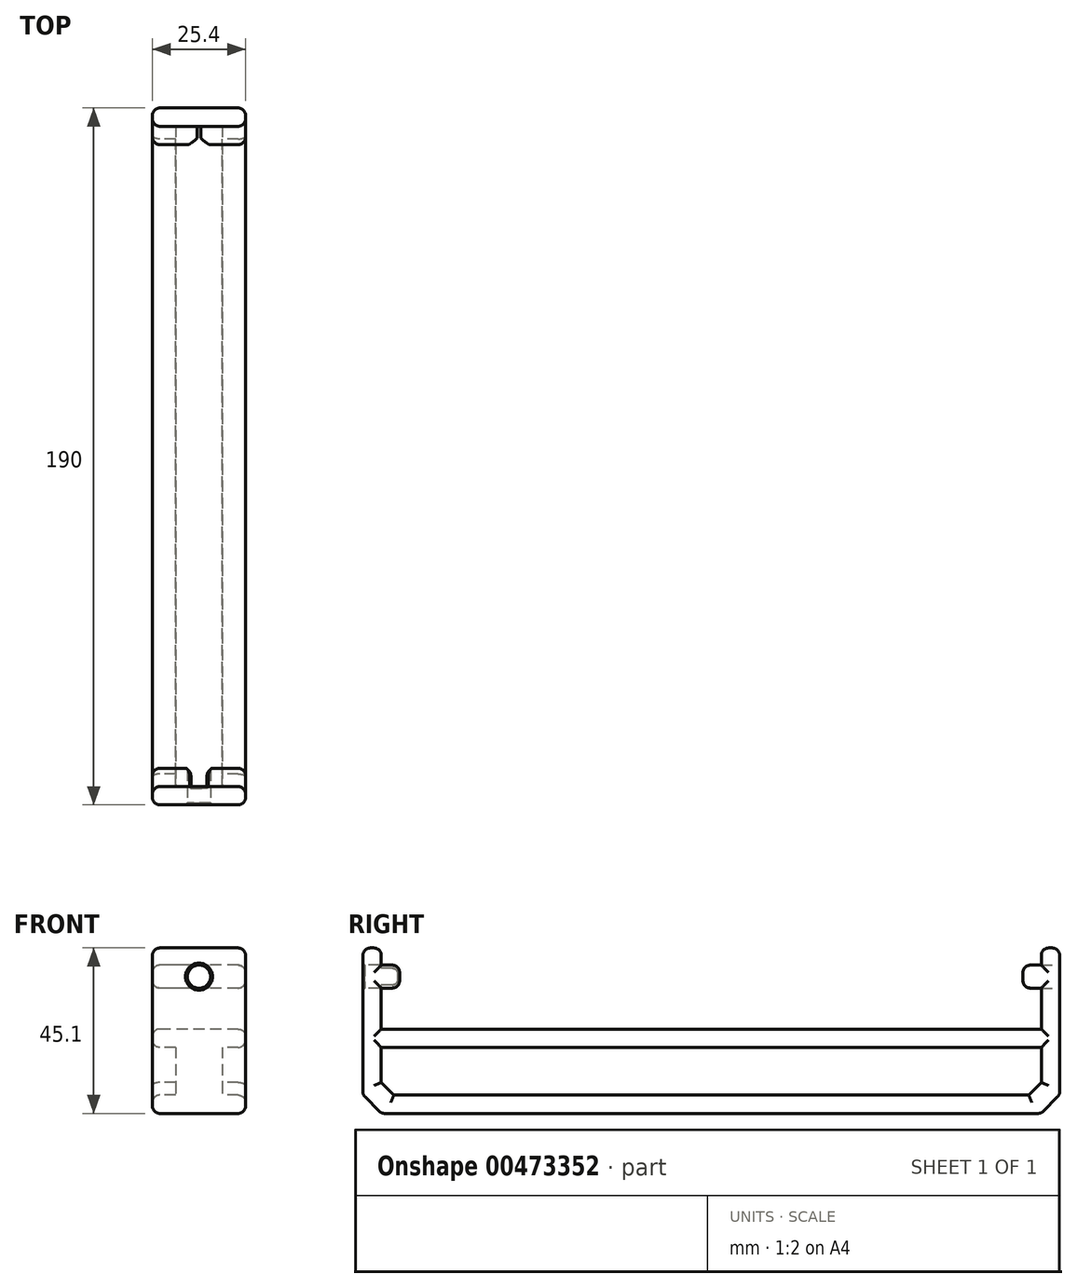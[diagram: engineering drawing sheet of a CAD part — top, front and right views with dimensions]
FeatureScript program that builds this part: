
annotation { "Feature Type Name" : "Feature", "Feature Type Description" : "" }
export const myFeature = defineFeature(function(context is Context, id is Id, definition is map)
    precondition{}
    {
        {
            var Q0;
            Q0=qCreatedBy(makeId("Right.planeOp"),FACE);
            var sketch = newSketch(context, id + "F0", { "sketchPlane" : qUnion([Q0])});
            skLineSegment(sketch, "E0.right", {"start": v(90, 22.1) * mm, "end": v(90, 17.42) * mm});
            skLineSegment(sketch, "E1.MirrorCS", {"start": v(90, 11.16) * mm, "end": v(85, 11.16) * mm});
            skLineSegment(sketch, "E2.MirrorCS", {"start": v(90, 17.42) * mm, "end": v(85, 17.42) * mm});
            skLineSegment(sketch, "E3.trimOffspring", {"start": v(90, 11.16) * mm, "end": v(90, 0) * mm});
            skLineSegment(sketch, "E4.bottom", {"start": v(90, 22.1) * mm, "end": v(95, 22.1) * mm});
            skLineSegment(sketch, "E5", {"start": v(95, 22.1) * mm, "end": v(95, -17.95) * mm});
            skLineSegment(sketch, "E6", {"start": v(89.95, -23) * mm, "end": v(0, -23) * mm});
            skLineSegment(sketch, "E7", {"start": v(90, -5) * mm, "end": v(0, -5) * mm});
            skLineSegment(sketch, "E8", {"start": v(86.57, -18) * mm, "end": v(0, -18) * mm});
            skLineSegment(sketch, "E9.trimOffspring", {"start": v(90, -5) * mm, "end": v(90, -14.57) * mm});
            skLineSegment(sketch, "E10", {"start": v(95, -17.95) * mm, "end": v(89.95, -23) * mm});
            skLineSegment(sketch, "E11", {"start": v(90, -14.57) * mm, "end": v(86.57, -18) * mm});
            skLineSegment(sketch, "E12", {"start": v(90, 0) * mm, "end": v(0, 0) * mm});
            skLineSegment(sketch, "E13.MirrorCS", {"start": v(-90, -5) * mm, "end": v(0, -5) * mm});
            skLineSegment(sketch, "E14.MirrorCS", {"start": v(-86.57, -18) * mm, "end": v(0, -18) * mm});
            skLineSegment(sketch, "E15.MirrorCS", {"start": v(-90, 22.1) * mm, "end": v(-95, 22.1) * mm});
            skLineSegment(sketch, "E16.MirrorCS", {"start": v(-95, -17.95) * mm, "end": v(-89.95, -23) * mm});
            skLineSegment(sketch, "E17.MirrorCS", {"start": v(-89.95, -23) * mm, "end": v(0, -23) * mm});
            skLineSegment(sketch, "E18.MirrorCS", {"start": v(-90, 11.16) * mm, "end": v(-90, 0) * mm});
            skLineSegment(sketch, "E19.MirrorCS", {"start": v(-90, -5) * mm, "end": v(-90, -14.57) * mm});
            skLineSegment(sketch, "E20.MirrorCS", {"start": v(-90, 0) * mm, "end": v(0, 0) * mm});
            skLineSegment(sketch, "E21.MirrorCS", {"start": v(-95, 22.1) * mm, "end": v(-95, -17.95) * mm});
            skLineSegment(sketch, "E22.MirrorCS", {"start": v(-90, 22.1) * mm, "end": v(-90, 17.42) * mm});
            skLineSegment(sketch, "E23.MirrorCS", {"start": v(-90, -14.57) * mm, "end": v(-86.57, -18) * mm});
            skLineSegment(sketch, "E24", {"start": v(85, 17.42) * mm, "end": v(85, 11.16) * mm});
            skPoint(sketch, "E25.MirrorCS.end.orphan", {"position": v(85, 17.42) * mm});
            skPoint(sketch, "E26.MirrorCS.end.orphan", {"position": v(85, 11.16) * mm});
            skLineSegment(sketch, "E27.MirrorCS", {"start": v(-85, 17.42) * mm, "end": v(-85, 11.16) * mm});
            skLineSegment(sketch, "E28.MirrorCS", {"start": v(-90, 17.42) * mm, "end": v(-85, 17.42) * mm});
            skLineSegment(sketch, "E29.MirrorCS", {"start": v(-90, 11.16) * mm, "end": v(-85, 11.16) * mm});
            skSolve(sketch);
        }
        {
            var Q0;
            Q0=makeQuery(id+"F0.imprint","IMPRINT",FACE,{"disambiguationData":[TD([[makeQuery(id+"F0.imprint","IMPRINT",EDGE,{"derivedFrom":sQuery(id+"F0.wireOp",EDGE,"E0.right")}),1.0]])]});
            extrude(context, id + "F1", {"entities" : qUnion([Q0]), "endBound" : BoundingType.SYMMETRIC, "depth" : 25.4 * mm});
        }
        {
            var Q0;
            {var subQ3=sQuery(id+"F0.wireOp",EDGE,"E7");Q0=makeQuery(id+"F0.imprint","IMPRINT",FACE,{"disambiguationData":[TD([[makeQuery(id+"F0.imprint","IMPRINT",EDGE,{"derivedFrom":subQ3}),1.0]])]});}
            extrude(context, id + "F2", {"entities" : qUnion([Q0]), "operationType" : NewBodyOperationType.ADD, "endBound" : BoundingType.SYMMETRIC, "depth" : 12.7 * mm});
        }
        {
            var Q0;
            Q0=makeQuery(id+"F1.opExtrude","SWEPT_EDGE",EDGE,{"disambiguationData":[OSD([sQuery(id+"F0.wireOp",EDGE,"0077e2ba-aa52-4f11-a289-9c433e1f9747.MirrorCS"),sQuery(id+"F0.wireOp",EDGE,"f951b748-9c31-433f-a569-38f65a587bd9.MirrorCS")])]});
            var Q1;
            Q1=makeQuery(id+"F1.opExtrude","SWEPT_EDGE",EDGE,{"disambiguationData":[OSD([sQuery(id+"F0.wireOp",EDGE,"1ec25f01-2b87-4167-9ce9-411135ac6d64.MirrorCS"),sQuery(id+"F0.wireOp",EDGE,"0077e2ba-aa52-4f11-a289-9c433e1f9747.MirrorCS")])]});
            var Q2;
            Q2=makeQuery(id+"F1.opExtrude","CAP_EDGE",EDGE,{"disambiguationData":[OSD([sQuery(id+"F0.wireOp",EDGE,"0077e2ba-aa52-4f11-a289-9c433e1f9747.MirrorCS")])],"isStart":false});
            var Q3;
            Q3=makeQuery(id+"F1.opExtrude","CAP_EDGE",EDGE,{"disambiguationData":[OSD([sQuery(id+"F0.wireOp",EDGE,"f951b748-9c31-433f-a569-38f65a587bd9.MirrorCS")])],"isStart":false});
            var Q4;
            Q4=makeQuery(id+"F1.opExtrude","CAP_EDGE",EDGE,{"disambiguationData":[OSD([sQuery(id+"F0.wireOp",EDGE,"1ec25f01-2b87-4167-9ce9-411135ac6d64.MirrorCS")])],"isStart":false});
            var Q5;
            Q5=makeQuery(id+"F1.opExtrude","CAP_EDGE",EDGE,{"disambiguationData":[OSD([sQuery(id+"F0.wireOp",EDGE,"f951b748-9c31-433f-a569-38f65a587bd9.MirrorCS")])],"isStart":true});
            var Q6;
            Q6=makeQuery(id+"F1.opExtrude","CAP_EDGE",EDGE,{"disambiguationData":[OSD([sQuery(id+"F0.wireOp",EDGE,"0077e2ba-aa52-4f11-a289-9c433e1f9747.MirrorCS")])],"isStart":true});
            var Q7;
            Q7=makeQuery(id+"F1.opExtrude","CAP_EDGE",EDGE,{"disambiguationData":[OSD([sQuery(id+"F0.wireOp",EDGE,"1ec25f01-2b87-4167-9ce9-411135ac6d64.MirrorCS")])],"isStart":true});
            var Q8;
            Q8=makeQuery(id+"F1.opExtrude","SWEPT_FACE",FACE,{"disambiguationData":[OSD([sQuery(id+"F0.wireOp",EDGE,"E5")])]});
            var Q9;
            Q9=makeQuery(id+"F1.opExtrude","CAP_EDGE",EDGE,{"disambiguationData":[OSD([sQuery(id+"F0.wireOp",EDGE,"E10")])],"isStart":true});
            var Q10;
            Q10=makeQuery(id+"F1.opExtrude","CAP_EDGE",EDGE,{"disambiguationData":[OSD([sQuery(id+"F0.wireOp",EDGE,"E10")])],"isStart":false});
            var Q11;
            Q11=makeQuery(id+"F1.opExtrude","SWEPT_EDGE",EDGE,{"disambiguationData":[OSD([sQuery(id+"F0.wireOp",EDGE,"E6"),sQuery(id+"F0.wireOp",EDGE,"E10")])]});
            var Q12;
            Q12=makeQuery(id+"F1.opExtrude","CAP_EDGE",EDGE,{"disambiguationData":[OSD([sQuery(id+"F0.wireOp",EDGE,"E6"),sQuery(id+"F0.wireOp",EDGE,"E17.MirrorCS")])],"isStart":false});
            var Q13;
            Q13=makeQuery(id+"F1.opExtrude","CAP_EDGE",EDGE,{"disambiguationData":[OSD([sQuery(id+"F0.wireOp",EDGE,"E6"),sQuery(id+"F0.wireOp",EDGE,"E17.MirrorCS")])],"isStart":true});
            var Q14;
            Q14=makeQuery(id+"F1.opExtrude","CAP_EDGE",EDGE,{"disambiguationData":[OSD([sQuery(id+"F0.wireOp",EDGE,"E4.bottom")])],"isStart":true});
            var Q15;
            Q15=makeQuery(id+"F1.opExtrude","CAP_EDGE",EDGE,{"disambiguationData":[OSD([sQuery(id+"F0.wireOp",EDGE,"E4.bottom")])],"isStart":false});
            var Q16;
            Q16=makeQuery(id+"F1.opExtrude","SWEPT_EDGE",EDGE,{"disambiguationData":[OSD([sQuery(id+"F0.wireOp",EDGE,"4332f96a-2dc4-4a46-8b67-e16dc0cf48052.MirrorCS"),sQuery(id+"F0.wireOp",EDGE,"E131.MirrorCS")])]});
            var Q17;
            Q17=makeQuery(id+"F1.opExtrude","CAP_EDGE",EDGE,{"disambiguationData":[OSD([sQuery(id+"F0.wireOp",EDGE,"E131.MirrorCS")])],"isStart":true});
            var Q18;
            Q18=makeQuery(id+"F1.opExtrude","CAP_EDGE",EDGE,{"disambiguationData":[OSD([sQuery(id+"F0.wireOp",EDGE,"E131.MirrorCS")])],"isStart":false});
            var Q19;
            Q19=makeQuery(id+"F1.opExtrude","CAP_EDGE",EDGE,{"disambiguationData":[OSD([sQuery(id+"F0.wireOp",EDGE,"4332f96a-2dc4-4a46-8b67-e16dc0cf48059.MirrorCS")])],"isStart":true});
            var Q20;
            Q20=makeQuery(id+"F1.opExtrude","CAP_EDGE",EDGE,{"disambiguationData":[OSD([sQuery(id+"F0.wireOp",EDGE,"4332f96a-2dc4-4a46-8b67-e16dc0cf48052.MirrorCS")])],"isStart":false});
            var Q21;
            Q21=makeQuery(id+"F1.opExtrude","SWEPT_EDGE",EDGE,{"disambiguationData":[OSD([sQuery(id+"F0.wireOp",EDGE,"4332f96a-2dc4-4a46-8b67-e16dc0cf48052.MirrorCS"),sQuery(id+"F0.wireOp",EDGE,"4332f96a-2dc4-4a46-8b67-e16dc0cf48059.MirrorCS")])]});
            var Q22;
            Q22=makeQuery(id+"F1.opExtrude","CAP_EDGE",EDGE,{"disambiguationData":[OSD([sQuery(id+"F0.wireOp",EDGE,"4332f96a-2dc4-4a46-8b67-e16dc0cf48052.MirrorCS")])],"isStart":true});
            var Q23;
            Q23=makeQuery(id+"F1.opExtrude","SWEPT_EDGE",EDGE,{"disambiguationData":[OSD([sQuery(id+"F0.wireOp",EDGE,"E15.MirrorCS"),sQuery(id+"F0.wireOp",EDGE,"E21.MirrorCS")])]});
            var Q24;
            Q24=makeQuery(id+"F1.opExtrude","CAP_EDGE",EDGE,{"disambiguationData":[OSD([sQuery(id+"F0.wireOp",EDGE,"E21.MirrorCS")])],"isStart":true});
            var Q25;
            Q25=makeQuery(id+"F1.opExtrude","CAP_EDGE",EDGE,{"disambiguationData":[OSD([sQuery(id+"F0.wireOp",EDGE,"E21.MirrorCS")])],"isStart":false});
            var Q26;
            Q26=makeQuery(id+"F1.opExtrude","SWEPT_EDGE",EDGE,{"disambiguationData":[OSD([sQuery(id+"F0.wireOp",EDGE,"E16.MirrorCS"),sQuery(id+"F0.wireOp",EDGE,"E21.MirrorCS")])]});
            var Q27;
            Q27=makeQuery(id+"F1.opExtrude","CAP_EDGE",EDGE,{"disambiguationData":[OSD([sQuery(id+"F0.wireOp",EDGE,"E16.MirrorCS")])],"isStart":true});
            var Q28;
            Q28=makeQuery(id+"F1.opExtrude","CAP_EDGE",EDGE,{"disambiguationData":[OSD([sQuery(id+"F0.wireOp",EDGE,"E16.MirrorCS")])],"isStart":false});
            var Q29;
            Q29=makeQuery(id+"F1.opExtrude","SWEPT_EDGE",EDGE,{"disambiguationData":[OSD([sQuery(id+"F0.wireOp",EDGE,"E16.MirrorCS"),sQuery(id+"F0.wireOp",EDGE,"E17.MirrorCS")])]});
            var Q30;
            Q30=makeQuery(id+"F1.opExtrude","CAP_EDGE",EDGE,{"disambiguationData":[OSD([sQuery(id+"F0.wireOp",EDGE,"E15.MirrorCS")])],"isStart":true});
            var Q31;
            Q31=makeQuery(id+"F1.opExtrude","CAP_EDGE",EDGE,{"disambiguationData":[OSD([sQuery(id+"F0.wireOp",EDGE,"E15.MirrorCS")])],"isStart":false});
            var Q32;
            Q32=makeQuery(id+"F1.opExtrude","CAP_EDGE",EDGE,{"disambiguationData":[OSD([sQuery(id+"F0.wireOp",EDGE,"4332f96a-2dc4-4a46-8b67-e16dc0cf48059.MirrorCS")])],"isStart":false});
            var Q33;
            Q33=makeQuery(id+"F1.opExtrude","SWEPT_EDGE",EDGE,{"disambiguationData":[OSD([sQuery(id+"F0.wireOp",EDGE,"E0.right"),sQuery(id+"F0.wireOp",EDGE,"E4.bottom")])]});
            var Q34;
            Q34=makeQuery(id+"F1.opExtrude","SWEPT_EDGE",EDGE,{"disambiguationData":[OSD([sQuery(id+"F0.wireOp",EDGE,"E15.MirrorCS"),sQuery(id+"F0.wireOp",EDGE,"E22.MirrorCS")])]});
            var Q35;
            Q35=makeQuery(id+"F1.opExtrude","CAP_EDGE",EDGE,{"disambiguationData":[OSD([sQuery(id+"F0.wireOp",EDGE,"E22.MirrorCS")])],"isStart":false});
            var Q36;
            Q36=makeQuery(id+"F1.opExtrude","CAP_EDGE",EDGE,{"disambiguationData":[OSD([sQuery(id+"F0.wireOp",EDGE,"4332f96a-2dc4-4a46-8b67-e16dc0cf48053.MirrorCS")])],"isStart":false});
            var Q37;
            Q37=makeQuery(id+"F1.opExtrude","CAP_EDGE",EDGE,{"disambiguationData":[OSD([sQuery(id+"F0.wireOp",EDGE,"b594eafc-073d-466a-81ae-7db81db10fd9.MirrorCS")])],"isStart":false});
            var Q38;
            Q38=makeQuery(id+"F1.opExtrude","CAP_EDGE",EDGE,{"disambiguationData":[OSD([sQuery(id+"F0.wireOp",EDGE,"E0.right")])],"isStart":false});
            var Q39;
            Q39=makeQuery(id+"F1.opExtrude","SWEPT_EDGE",EDGE,{"disambiguationData":[OSD([sQuery(id+"F0.wireOp",EDGE,"f951b748-9c31-433f-a569-38f65a587bd9.MirrorCS"),sQuery(id+"F0.wireOp",EDGE,"b594eafc-073d-466a-81ae-7db81db10fd9.MirrorCS")])]});
            var Q40;
            Q40=makeQuery(id+"F1.opExtrude","SWEPT_EDGE",EDGE,{"disambiguationData":[OSD([sQuery(id+"F0.wireOp",EDGE,"4332f96a-2dc4-4a46-8b67-e16dc0cf48053.MirrorCS"),sQuery(id+"F0.wireOp",EDGE,"E131.MirrorCS")])]});
            var Q41;
            Q41=makeQuery(id+"F1.opExtrude","CAP_EDGE",EDGE,{"disambiguationData":[OSD([sQuery(id+"F0.wireOp",EDGE,"E2.MirrorCS")])],"isStart":false});
            var Q42;
            Q42=makeQuery(id+"F1.opExtrude","CAP_EDGE",EDGE,{"disambiguationData":[OSD([sQuery(id+"F0.wireOp",EDGE,"4332f96a-2dc4-4a46-8b67-e16dc0cf48055.MirrorCS")])],"isStart":false});
            var Q43;
            Q43=makeQuery(id+"F1.opExtrude","CAP_EDGE",EDGE,{"disambiguationData":[OSD([sQuery(id+"F0.wireOp",EDGE,"E18.MirrorCS")])],"isStart":false});
            var Q44;
            Q44=makeQuery(id+"F1.opExtrude","CAP_EDGE",EDGE,{"disambiguationData":[OSD([sQuery(id+"F0.wireOp",EDGE,"E19.MirrorCS")])],"isStart":false});
            var Q45;
            Q45=makeQuery(id+"F1.opExtrude","CAP_EDGE",EDGE,{"disambiguationData":[OSD([sQuery(id+"F0.wireOp",EDGE,"4332f96a-2dc4-4a46-8b67-e16dc0cf48050.MirrorCS")])],"isStart":false});
            var Q46;
            Q46=makeQuery(id+"F1.opExtrude","CAP_EDGE",EDGE,{"disambiguationData":[OSD([sQuery(id+"F0.wireOp",EDGE,"E130.MirrorCS")])],"isStart":false});
            var Q47;
            Q47=makeQuery(id+"F1.opExtrude","CAP_EDGE",EDGE,{"disambiguationData":[OSD([sQuery(id+"F0.wireOp",EDGE,"E12"),sQuery(id+"F0.wireOp",EDGE,"E20.MirrorCS")])],"isStart":false});
            var Q48;
            Q48=makeQuery(id+"F1.opExtrude","CAP_EDGE",EDGE,{"disambiguationData":[OSD([sQuery(id+"F0.wireOp",EDGE,"E7"),sQuery(id+"F0.wireOp",EDGE,"E13.MirrorCS")])],"isStart":false});
            var Q49;
            Q49=makeQuery(id+"F1.opExtrude","SWEPT_EDGE",EDGE,{"disambiguationData":[OSD([sQuery(id+"F0.wireOp",EDGE,"4332f96a-2dc4-4a46-8b67-e16dc0cf48059.MirrorCS"),sQuery(id+"F0.wireOp",EDGE,"E130.MirrorCS")])]});
            var Q50;
            Q50=makeQuery(id+"F1.opExtrude","CAP_EDGE",EDGE,{"disambiguationData":[OSD([sQuery(id+"F0.wireOp",EDGE,"E23.MirrorCS")])],"isStart":false});
            var Q51;
            Q51=makeQuery(id+"F1.opExtrude","CAP_EDGE",EDGE,{"disambiguationData":[OSD([sQuery(id+"F0.wireOp",EDGE,"E8"),sQuery(id+"F0.wireOp",EDGE,"E14.MirrorCS")])],"isStart":false});
            var Q52;
            Q52=makeQuery(id+"F1.opExtrude","CAP_EDGE",EDGE,{"disambiguationData":[OSD([sQuery(id+"F0.wireOp",EDGE,"8f657946-5524-44a2-9e8d-38776d1434ba.MirrorCS")])],"isStart":false});
            var Q53;
            Q53=makeQuery(id+"F1.opExtrude","CAP_EDGE",EDGE,{"disambiguationData":[OSD([sQuery(id+"F0.wireOp",EDGE,"E1.MirrorCS")])],"isStart":false});
            var Q54;
            Q54=makeQuery(id+"F1.opExtrude","CAP_EDGE",EDGE,{"disambiguationData":[OSD([sQuery(id+"F0.wireOp",EDGE,"E3.trimOffspring")])],"isStart":false});
            var Q55;
            Q55=makeQuery(id+"F1.opExtrude","SWEPT_EDGE",EDGE,{"disambiguationData":[OSD([sQuery(id+"F0.wireOp",EDGE,"1ec25f01-2b87-4167-9ce9-411135ac6d64.MirrorCS"),sQuery(id+"F0.wireOp",EDGE,"8f657946-5524-44a2-9e8d-38776d1434ba.MirrorCS")])]});
            var Q56;
            Q56=makeQuery(id+"F1.opExtrude","CAP_EDGE",EDGE,{"disambiguationData":[OSD([sQuery(id+"F0.wireOp",EDGE,"E11")])],"isStart":false});
            var Q57;
            Q57=makeQuery(id+"F1.opExtrude","CAP_EDGE",EDGE,{"disambiguationData":[OSD([sQuery(id+"F0.wireOp",EDGE,"E9.trimOffspring")])],"isStart":false});
            var Q58;
            Q58=makeQuery(id+"F1.opExtrude","CAP_EDGE",EDGE,{"disambiguationData":[OSD([sQuery(id+"F0.wireOp",EDGE,"b594eafc-073d-466a-81ae-7db81db10fd9.MirrorCS")])],"isStart":true});
            var Q59;
            Q59=makeQuery(id+"F1.opExtrude","CAP_EDGE",EDGE,{"disambiguationData":[OSD([sQuery(id+"F0.wireOp",EDGE,"E0.right")])],"isStart":true});
            var Q60;
            Q60=makeQuery(id+"F1.opExtrude","CAP_EDGE",EDGE,{"disambiguationData":[OSD([sQuery(id+"F0.wireOp",EDGE,"E2.MirrorCS")])],"isStart":true});
            var Q61;
            Q61=makeQuery(id+"F1.opExtrude","CAP_EDGE",EDGE,{"disambiguationData":[OSD([sQuery(id+"F0.wireOp",EDGE,"E1.MirrorCS")])],"isStart":true});
            var Q62;
            Q62=makeQuery(id+"F1.opExtrude","CAP_EDGE",EDGE,{"disambiguationData":[OSD([sQuery(id+"F0.wireOp",EDGE,"8f657946-5524-44a2-9e8d-38776d1434ba.MirrorCS")])],"isStart":true});
            var Q63;
            Q63=makeQuery(id+"F1.opExtrude","CAP_EDGE",EDGE,{"disambiguationData":[OSD([sQuery(id+"F0.wireOp",EDGE,"E3.trimOffspring")])],"isStart":true});
            var Q64;
            Q64=makeQuery(id+"F1.opExtrude","CAP_EDGE",EDGE,{"disambiguationData":[OSD([sQuery(id+"F0.wireOp",EDGE,"E9.trimOffspring")])],"isStart":true});
            var Q65;
            Q65=makeQuery(id+"F1.opExtrude","CAP_EDGE",EDGE,{"disambiguationData":[OSD([sQuery(id+"F0.wireOp",EDGE,"E11")])],"isStart":true});
            var Q66;
            Q66=makeQuery(id+"F1.opExtrude","CAP_EDGE",EDGE,{"disambiguationData":[OSD([sQuery(id+"F0.wireOp",EDGE,"E8"),sQuery(id+"F0.wireOp",EDGE,"E14.MirrorCS")])],"isStart":true});
            var Q67;
            Q67=makeQuery(id+"F1.opExtrude","CAP_EDGE",EDGE,{"disambiguationData":[OSD([sQuery(id+"F0.wireOp",EDGE,"E7"),sQuery(id+"F0.wireOp",EDGE,"E13.MirrorCS")])],"isStart":true});
            var Q68;
            Q68=makeQuery(id+"F1.opExtrude","CAP_EDGE",EDGE,{"disambiguationData":[OSD([sQuery(id+"F0.wireOp",EDGE,"E12"),sQuery(id+"F0.wireOp",EDGE,"E20.MirrorCS")])],"isStart":true});
            var Q69;
            Q69=makeQuery(id+"F1.opExtrude","CAP_EDGE",EDGE,{"disambiguationData":[OSD([sQuery(id+"F0.wireOp",EDGE,"E19.MirrorCS")])],"isStart":true});
            var Q70;
            Q70=makeQuery(id+"F1.opExtrude","CAP_EDGE",EDGE,{"disambiguationData":[OSD([sQuery(id+"F0.wireOp",EDGE,"E23.MirrorCS")])],"isStart":true});
            var Q71;
            Q71=makeQuery(id+"F1.opExtrude","CAP_EDGE",EDGE,{"disambiguationData":[OSD([sQuery(id+"F0.wireOp",EDGE,"E18.MirrorCS")])],"isStart":true});
            var Q72;
            Q72=makeQuery(id+"F1.opExtrude","CAP_EDGE",EDGE,{"disambiguationData":[OSD([sQuery(id+"F0.wireOp",EDGE,"4332f96a-2dc4-4a46-8b67-e16dc0cf48050.MirrorCS")])],"isStart":true});
            var Q73;
            Q73=makeQuery(id+"F1.opExtrude","CAP_EDGE",EDGE,{"disambiguationData":[OSD([sQuery(id+"F0.wireOp",EDGE,"E22.MirrorCS")])],"isStart":true});
            var Q74;
            Q74=makeQuery(id+"F1.opExtrude","CAP_EDGE",EDGE,{"disambiguationData":[OSD([sQuery(id+"F0.wireOp",EDGE,"4332f96a-2dc4-4a46-8b67-e16dc0cf48055.MirrorCS")])],"isStart":true});
            var Q75;
            Q75=makeQuery(id+"F1.opExtrude","CAP_EDGE",EDGE,{"disambiguationData":[OSD([sQuery(id+"F0.wireOp",EDGE,"4332f96a-2dc4-4a46-8b67-e16dc0cf48053.MirrorCS")])],"isStart":true});
            var Q76;
            Q76=makeQuery(id+"F1.opExtrude","CAP_EDGE",EDGE,{"disambiguationData":[OSD([sQuery(id+"F0.wireOp",EDGE,"E130.MirrorCS")])],"isStart":true});
            var Q77;
            Q77=makeQuery(id+"F1.opExtrude","CAP_EDGE",EDGE,{"disambiguationData":[OSD([sQuery(id+"F0.wireOp",EDGE,"E24")])],"isStart":true});
            var Q78;
            Q78=makeQuery(id+"F1.opExtrude","SWEPT_EDGE",EDGE,{"disambiguationData":[OSD([sQuery(id+"F0.wireOp",EDGE,"E2.MirrorCS"),sQuery(id+"F0.wireOp",EDGE,"E24")])]});
            var Q79;
            Q79=makeQuery(id+"F1.opExtrude","CAP_EDGE",EDGE,{"disambiguationData":[OSD([sQuery(id+"F0.wireOp",EDGE,"E24")])],"isStart":false});
            var Q80;
            Q80=makeQuery(id+"F1.opExtrude","SWEPT_EDGE",EDGE,{"disambiguationData":[OSD([sQuery(id+"F0.wireOp",EDGE,"E1.MirrorCS"),sQuery(id+"F0.wireOp",EDGE,"E24")])]});
            var Q81;
            Q81=makeQuery(id+"F1.opExtrude","CAP_EDGE",EDGE,{"disambiguationData":[OSD([sQuery(id+"F0.wireOp",EDGE,"E28.MirrorCS")])],"isStart":false});
            var Q82;
            Q82=makeQuery(id+"F1.opExtrude","SWEPT_EDGE",EDGE,{"disambiguationData":[OSD([sQuery(id+"F0.wireOp",EDGE,"E27.MirrorCS"),sQuery(id+"F0.wireOp",EDGE,"E29.MirrorCS")])]});
            var Q83;
            Q83=makeQuery(id+"F1.opExtrude","SWEPT_EDGE",EDGE,{"disambiguationData":[OSD([sQuery(id+"F0.wireOp",EDGE,"E27.MirrorCS"),sQuery(id+"F0.wireOp",EDGE,"E28.MirrorCS")])]});
            var Q84;
            Q84=makeQuery(id+"F1.opExtrude","CAP_EDGE",EDGE,{"disambiguationData":[OSD([sQuery(id+"F0.wireOp",EDGE,"E27.MirrorCS")])],"isStart":false});
            var Q85;
            Q85=makeQuery(id+"F1.opExtrude","CAP_EDGE",EDGE,{"disambiguationData":[OSD([sQuery(id+"F0.wireOp",EDGE,"E29.MirrorCS")])],"isStart":false});
            var Q86;
            Q86=makeQuery(id+"F1.opExtrude","CAP_EDGE",EDGE,{"disambiguationData":[OSD([sQuery(id+"F0.wireOp",EDGE,"E27.MirrorCS")])],"isStart":true});
            var Q87;
            Q87=makeQuery(id+"F1.opExtrude","CAP_EDGE",EDGE,{"disambiguationData":[OSD([sQuery(id+"F0.wireOp",EDGE,"E28.MirrorCS")])],"isStart":true});
            var Q88;
            Q88=makeQuery(id+"F1.opExtrude","CAP_EDGE",EDGE,{"disambiguationData":[OSD([sQuery(id+"F0.wireOp",EDGE,"E29.MirrorCS")])],"isStart":true});
            fillet(context, id + "F3", {"entities" : qUnion([Q0, Q1, Q2, Q3, Q4, Q5, Q6, Q7, Q8, Q9, Q10, Q11, Q12, Q13, Q14, Q15, Q16, Q17, Q18, Q19, Q20, Q21, Q22, Q23, Q24, Q25, Q26, Q27, Q28, Q29, Q30, Q31, Q32, Q33, Q34, Q35, Q36, Q37, Q38, Q39, Q40, Q41, Q42, Q43, Q44, Q45, Q46, Q47, Q48, Q49, Q50, Q51, Q52, Q53, Q54, Q55, Q56, Q57, Q58, Q59, Q60, Q61, Q62, Q63, Q64, Q65, Q66, Q67, Q68, Q69, Q70, Q71, Q72, Q73, Q74, Q75, Q76, Q77, Q78, Q79, Q80, Q81, Q82, Q83, Q84, Q85, Q86, Q87, Q88]), "radius" : 2 * mm, "tangentPropagation" : true, "allowEdgeOverflow" : false});
        }
        {
            var Q0;
            Q0=makeQuery(id+"F1.opExtrude","SWEPT_FACE",FACE,{"disambiguationData":[OSD([sQuery(id+"F0.wireOp",EDGE,"E5")])]});
            var sketch = newSketch(context, id + "F4", { "sketchPlane" : qUnion([Q0])});
            skCircle(sketch, "E30", {"center": v(0, 14.28) * mm, "radius": 3.17 * mm});
            skSolve(sketch);
        }
        {
            var Q0;
            Q0=makeQuery(id+"F4.imprint","IMPRINT",FACE,{"disambiguationData":[TD([[makeQuery(id+"F4.imprint","IMPRINT",EDGE,{"derivedFrom":sQuery(id+"F4.wireOp",EDGE,"E30")}),1.0]])]});
            extrude(context, id + "F5", {"entities" : qUnion([Q0]), "operationType" : NewBodyOperationType.REMOVE, "oppositeDirection" : true, "depth" : 25 * mm});
        }
        {
            var Q0;
            Q0=makeQuery(id+"F1.opExtrude","SWEPT_FACE",FACE,{"disambiguationData":[OSD([sQuery(id+"F0.wireOp",EDGE,"E21.MirrorCS")])]});
            var sketch = newSketch(context, id + "F6", { "sketchPlane" : qUnion([Q0])});
            skCircle(sketch, "E31", {"center": v(0, 14.28) * mm, "radius": 3.17 * mm});
            skSolve(sketch);
        }
        {
            var Q0;
            Q0 = qSketchRegion(id + "F6", true);
            extrude(context, id + "F7", {"entities" : qUnion([Q0]), "operationType" : NewBodyOperationType.REMOVE, "oppositeDirection" : true, "depth" : 25 * mm});
        }
        {
            var Q0;
            Q0=makeQuery(id+"F5.boolean.opBoolean","COPY",EDGE,{"derivedFrom":makeQuery(id+"F5.opExtrude","CAP_EDGE",EDGE,{"disambiguationData":[OSD([sQuery(id+"F4.wireOp",EDGE,"E30")])],"isStart":true})});
            var Q1;
            Q1=makeQuery(id+"F7.boolean.opBoolean","COPY",FACE,{"derivedFrom":makeQuery(id+"F7.opExtrude","SWEPT_FACE",FACE,{"disambiguationData":[OSD([sQuery(id+"F6.wireOp",EDGE,"E31")])]})});
            chamfer(context, id + "F8", {"entities" : qUnion([Q0, Q1]), "width" : .5 * mm, "tangentPropagation" : true});
        }
    });
